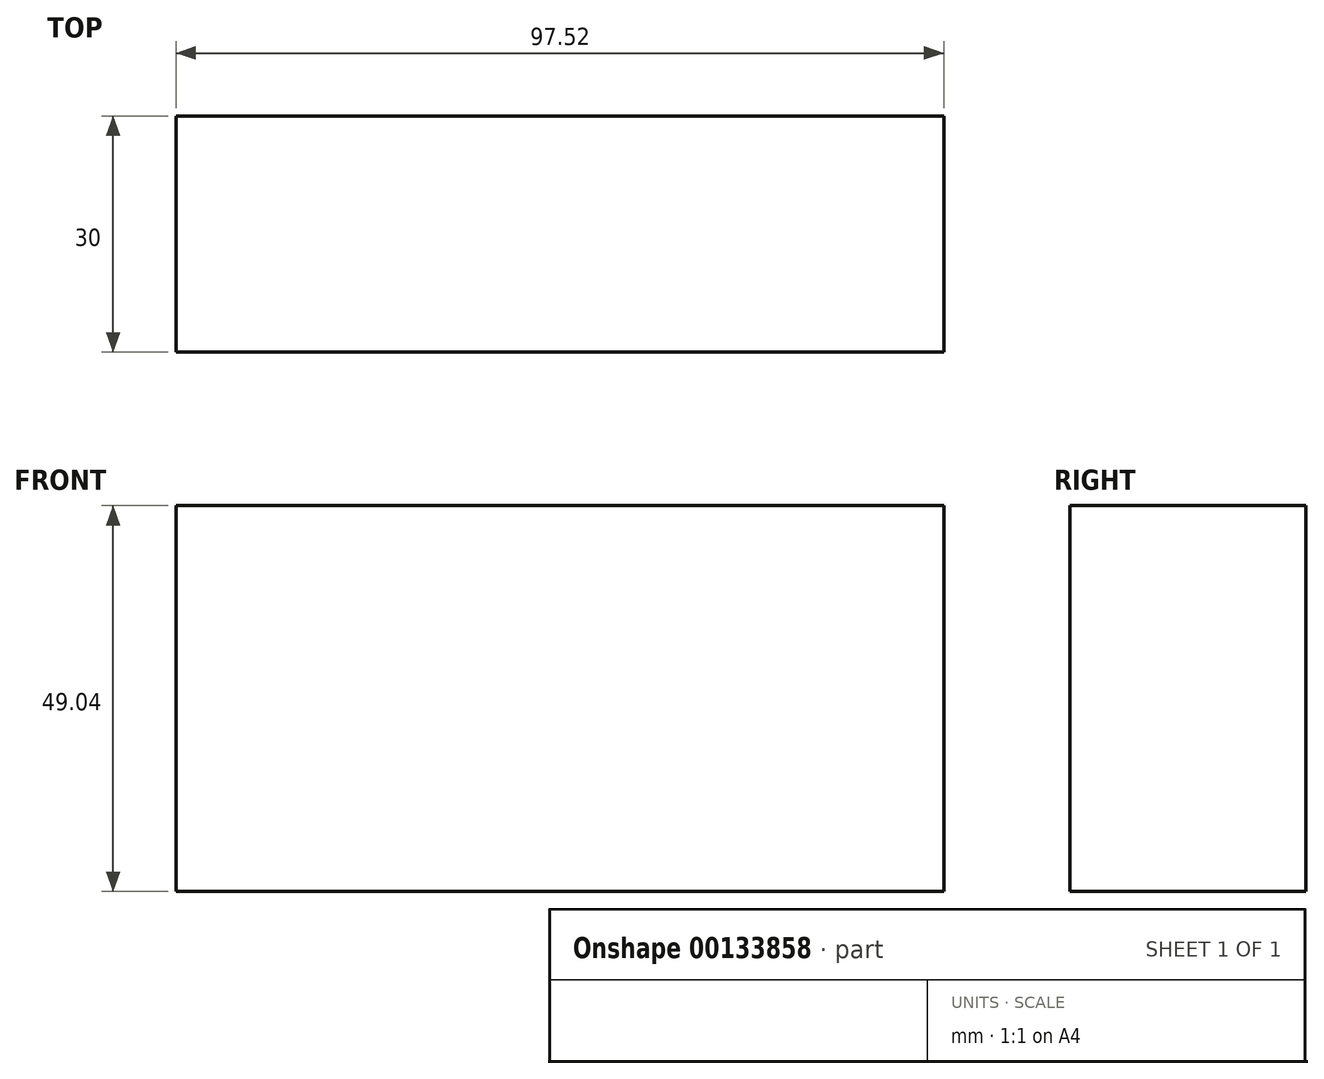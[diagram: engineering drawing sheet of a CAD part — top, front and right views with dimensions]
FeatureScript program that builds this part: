
annotation { "Feature Type Name" : "Feature", "Feature Type Description" : "" }
export const myFeature = defineFeature(function(context is Context, id is Id, definition is map)
    precondition{}
    {
        {
            var Q0;
            Q0=qCreatedBy(makeId("Front.planeOp"),FACE);
            var sketch = newSketch(context, id + "F0", { "sketchPlane" : qUnion([Q0])});
            skLineSegment(sketch, "E0.bottom", {"start": v(-48.76, -24.52) * mm, "end": v(48.76, -24.52) * mm});
            skLineSegment(sketch, "E0.top", {"start": v(-48.76, 24.52) * mm, "end": v(48.76, 24.52) * mm});
            skLineSegment(sketch, "E0.left", {"start": v(-48.76, -24.52) * mm, "end": v(-48.76, 24.52) * mm});
            skLineSegment(sketch, "E0.right", {"start": v(48.76, -24.52) * mm, "end": v(48.76, 24.52) * mm});
            skPoint(sketch, "E0.middle", {"position": v(0, 0) * mm});
            skLineSegment(sketch, "E1.bottom", {"start": v(66.23, 76.47) * mm, "end": v(123.43, 76.47) * mm});
            skLineSegment(sketch, "E1.top", {"start": v(66.23, 101.9) * mm, "end": v(123.43, 101.9) * mm});
            skLineSegment(sketch, "E1.left", {"start": v(66.23, 76.47) * mm, "end": v(66.23, 101.9) * mm});
            skLineSegment(sketch, "E1.right", {"start": v(123.43, 76.47) * mm, "end": v(123.43, 101.9) * mm});
            skPoint(sketch, "E1.middle", {"position": v(94.83, 89.18) * mm});
            skLineSegment(sketch, "E2", {"start": v(48.76, 24.52) * mm, "end": v(48.76, 68.36) * mm});
            skArc(sketch, "E3", {"start": v(48.76, 68.36) * mm, "mid": v(52.35, 77.02) * mm, "end": v(61.02, 80.61) * mm});
            skLineSegment(sketch, "E4", {"start": v(61.02, 80.61) * mm, "end": v(104.37, 80.61) * mm});
            skSolve(sketch);
        }
        {
            var Q0;
            Q0=makeQuery(id+"F0.imprint","IMPRINT",FACE,{"disambiguationData":[TD([[makeQuery(id+"F0.imprint","IMPRINT",EDGE,{"derivedFrom":sQuery(id+"F0.wireOp",EDGE,"E0.bottom")}),1.0]])]});
            var sketch = newSketch(context, id + "F1", { "sketchPlane" : qUnion([Q0])});
            skSolve(sketch);
        }
        {
            var Q0;
            Q0=makeQuery(id+"F1.imprint","IMPRINT",FACE,{"disambiguationData":[TD([[makeQuery(id+"F1.imprint","IMPRINT",EDGE,{"derivedFrom":makeQuery(id+"F0.imprint","IMPRINT",EDGE,{"derivedFrom":sQuery(id+"F0.wireOp",EDGE,"E0.bottom")})}),1.0]])]});
            extrude(context, id + "F2", {"entities" : qUnion([Q0]), "depth" : 30 * mm});
        }
    });
